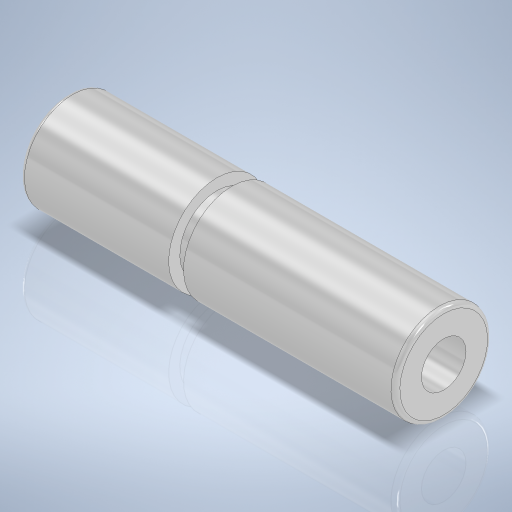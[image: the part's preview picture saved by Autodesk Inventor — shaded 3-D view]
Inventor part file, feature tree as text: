
AUTODESK INVENTOR PART (.ipt)
format: ipt  version: 2024 (Build 280153000, 153)  size: 289,280 bytes
history: native  units: mm
features: sketch x2, revolve x1, hole x1, fillet x1
ambient origin geometry x8: Origin, YZ Plane, XZ Plane, XY Plane, X Axis, Y Axis, Z Axis, Center Point
bodies: Volumenkörper1 (feature_tree)
feature tree (5):
  revolve  "Umdrehung1"
  hole  "Bohrung1"  [1 undecoded]
  fillet  "Rundung1"  Radius=2.0mm
  sketch  "Skizze1"  dims[d0=13.0mm d1=20.0mm d2=2.0mm]
  sketch  "Skizze2"  dims[d3=28.5mm d4=10.0mm d5=90.0deg d6=6.0mm d7=6.0mm d8=4.0mm d9=2.0mm d10=90.0deg d11=8.0mm d12=20.594885mm d13=0.6mm]
note: 1 required parameter value undecoded (feature->parameter linkage not recoverable at this tier; creation-order binding heuristic only, values carry confidence <= 0.55)
